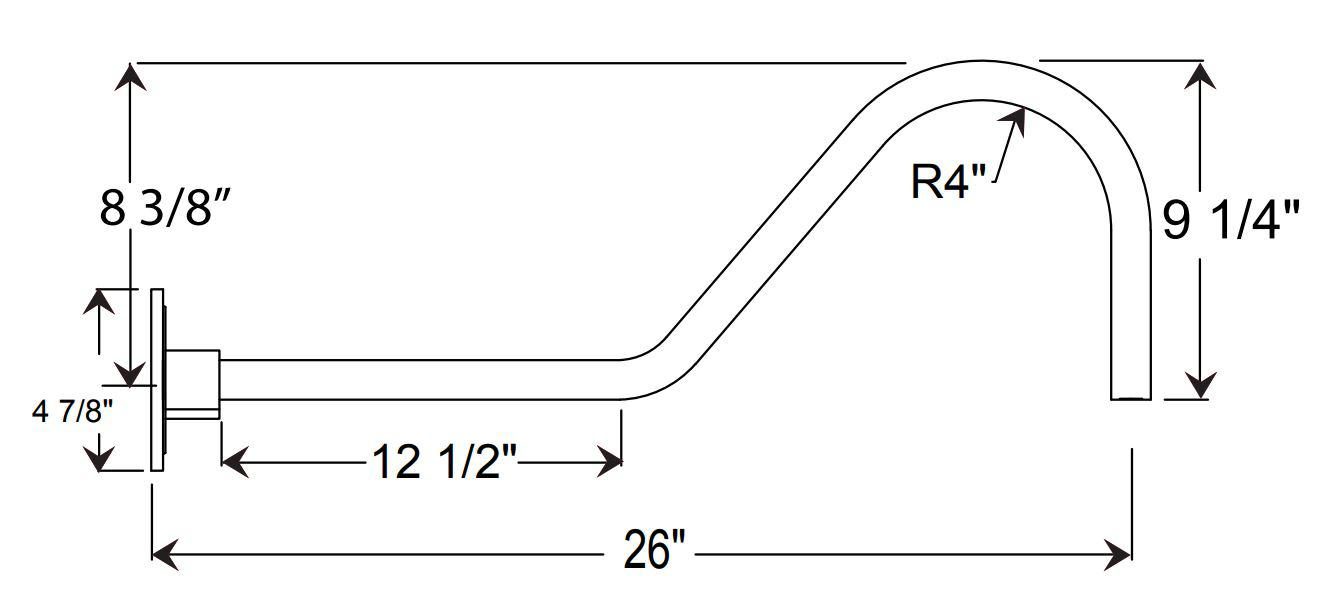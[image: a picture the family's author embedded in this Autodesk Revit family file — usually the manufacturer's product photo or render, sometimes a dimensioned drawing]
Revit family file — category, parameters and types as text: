
# Revit family: OSOC LED 20
name_source: partatom
category: Lighting Fixtures
units: mm (PartAtom-declared; Revit-internal decimal feet)

## family parameters
Always vertical = Yes
Cut with Voids When Loaded = No
Light Source = Yes
OmniClass Number = 23.80.70.00
OmniClass Title = Lighting
Part Type = Normal
Room Calculation Point = No
Round Connector Dimension = Use Diameter
Shared = No
Work Plane-Based = No

## types (1)
- OSOC20
    Apparent Load = 37 VA
    Body Colour = Spun aluminium
    Body Material = body
    CRI = >90
    Canopy Body = body
    Color Filter = 16777215
    Construction Material = Heavy Duty spun aluminum.
    Default Elevation = 0' - 0"
    Description = 120-277 Voltage
    Dimming = 1%
    Dimming Lamp Color Temperature Shift = <None>
    Efficiency = 65-125 lumens per watt
    Fixture Diameter = 1' - 8"
    Fixture Height = 1' - 7 3/4"
    GLASS = Glass
    HUB = body
    Lamp = LED
    Life = L70 50,000 hours
    Load Classification = Lighting
    Manufacturer = ANP Lighting
    Model = OSOC20
    OSOC20 = Yes
    Photometric Web File = generic
    Power Factor = 1
    Ring = body
    Tilt Angle = 90.00°
    URL = https://www.anplighting.com
    Voltage = 120 V
    Warranty = 5 year limited warranty
    Wattage Comments = 37 W
    Weight = 18.0 lbs
    a = 1' - 7"
    b = 0' - 3"

## geometry (parser evidence)
native form markers: Sweep x22
no freeform markers — native parametric forms only
